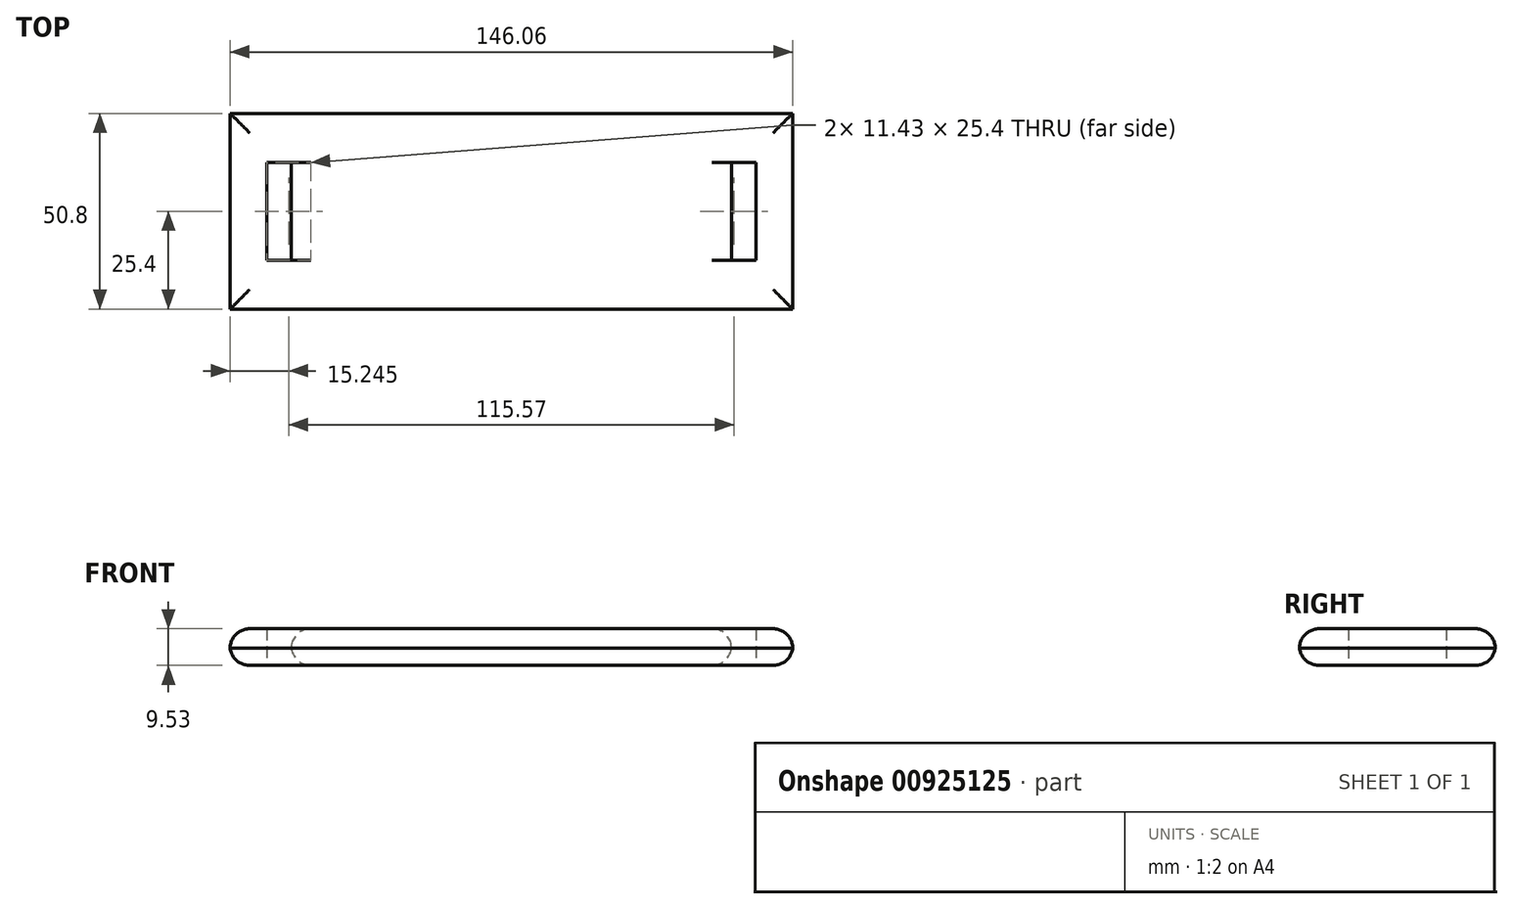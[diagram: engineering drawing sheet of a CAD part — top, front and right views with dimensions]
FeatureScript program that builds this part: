
annotation { "Feature Type Name" : "Feature", "Feature Type Description" : "" }
export const myFeature = defineFeature(function(context is Context, id is Id, definition is map)
    precondition{}
    {
        {
            var Q0;
            Q0=qCreatedBy(makeId("Top.planeOp"),FACE);
            var sketch = newSketch(context, id + "F0", { "sketchPlane" : qUnion([Q0])});
            skLineSegment(sketch, "E0.bottom", {"start": v(73.03, -25.4) * mm, "end": v(-73.03, -25.4) * mm});
            skLineSegment(sketch, "E0.top", {"start": v(73.03, 25.4) * mm, "end": v(-73.03, 25.4) * mm});
            skLineSegment(sketch, "E0.left", {"start": v(73.03, -25.4) * mm, "end": v(73.03, 25.4) * mm});
            skLineSegment(sketch, "E0.right", {"start": v(-73.03, -25.4) * mm, "end": v(-73.03, 25.4) * mm});
            skPoint(sketch, "E0.middle", {"position": v(0, 0) * mm});
            skLineSegment(sketch, "E1.bottom", {"start": v(-57.15, -12.7) * mm, "end": v(-63.5, -12.7) * mm});
            skLineSegment(sketch, "E1.top", {"start": v(-57.15, 12.7) * mm, "end": v(-63.5, 12.7) * mm});
            skLineSegment(sketch, "E1.left", {"start": v(-57.15, -12.7) * mm, "end": v(-57.15, 12.7) * mm});
            skLineSegment(sketch, "E1.right", {"start": v(-63.5, -12.7) * mm, "end": v(-63.5, 12.7) * mm});
            skPoint(sketch, "E1.middle", {"position": v(-60.33, 0) * mm});
            skLineSegment(sketch, "E2.bottom", {"start": v(63.5, -12.7) * mm, "end": v(57.15, -12.7) * mm});
            skLineSegment(sketch, "E2.top", {"start": v(63.5, 12.7) * mm, "end": v(57.15, 12.7) * mm});
            skLineSegment(sketch, "E2.left", {"start": v(63.5, -12.7) * mm, "end": v(63.5, 12.7) * mm});
            skLineSegment(sketch, "E2.right", {"start": v(57.15, -12.7) * mm, "end": v(57.15, 12.7) * mm});
            skPoint(sketch, "E2.middle", {"position": v(60.32, 0) * mm});
            skSolve(sketch);
        }
        {
            var Q0;
            Q0 = qSketchRegion(id + "F0", true);
            extrude(context, id + "F1", {"entities" : qUnion([Q0]), "depth" : 9.52 * mm, "offsetDistance" : 25.4 * mm});
        }
        {
            var Q0;
            Q0=makeQuery(id+"F1.opExtrude","CAP_EDGE",EDGE,{"disambiguationData":[OSD([sQuery(id+"F0.wireOp",EDGE,"E0.top")])],"isStart":false});
            var Q1;
            Q1=makeQuery(id+"F1.opExtrude","CAP_EDGE",EDGE,{"disambiguationData":[OSD([sQuery(id+"F0.wireOp",EDGE,"E0.left")])],"isStart":false});
            var Q2;
            Q2=makeQuery(id+"F1.opExtrude","CAP_EDGE",EDGE,{"disambiguationData":[OSD([sQuery(id+"F0.wireOp",EDGE,"E0.bottom")])],"isStart":false});
            var Q3;
            Q3=makeQuery(id+"F1.opExtrude","CAP_EDGE",EDGE,{"disambiguationData":[OSD([sQuery(id+"F0.wireOp",EDGE,"E0.right")])],"isStart":false});
            fillet(context, id + "F2", {"entities" : qUnion([Q0, Q1, Q2, Q3]), "radius" : 5.08 * mm, "tangentPropagation" : true, "allowEdgeOverflow" : false});
        }
        {
            var Q0;
            Q0=makeQuery(id+"F1.opExtrude","CAP_EDGE",EDGE,{"disambiguationData":[OSD([sQuery(id+"F0.wireOp",EDGE,"E0.bottom")])],"isStart":true});
            var Q1;
            Q1=makeQuery(id+"F1.opExtrude","CAP_EDGE",EDGE,{"disambiguationData":[OSD([sQuery(id+"F0.wireOp",EDGE,"E0.right")])],"isStart":true});
            var Q2;
            Q2=makeQuery(id+"F1.opExtrude","CAP_EDGE",EDGE,{"disambiguationData":[OSD([sQuery(id+"F0.wireOp",EDGE,"E0.top")])],"isStart":true});
            var Q3;
            Q3=makeQuery(id+"F1.opExtrude","CAP_EDGE",EDGE,{"disambiguationData":[OSD([sQuery(id+"F0.wireOp",EDGE,"E0.left")])],"isStart":true});
            var Q4;
            Q4=makeQuery(id+"F1.opExtrude","CAP_EDGE",EDGE,{"disambiguationData":[OSD([sQuery(id+"F0.wireOp",EDGE,"E2.right")])],"isStart":false});
            var Q5;
            Q5=makeQuery(id+"F1.opExtrude","CAP_EDGE",EDGE,{"disambiguationData":[OSD([sQuery(id+"F0.wireOp",EDGE,"E2.right")])],"isStart":true});
            var Q6;
            Q6=makeQuery(id+"F1.opExtrude","CAP_EDGE",EDGE,{"disambiguationData":[OSD([sQuery(id+"F0.wireOp",EDGE,"E1.left")])],"isStart":false});
            var Q7;
            Q7=makeQuery(id+"F1.opExtrude","CAP_EDGE",EDGE,{"disambiguationData":[OSD([sQuery(id+"F0.wireOp",EDGE,"E1.left")])],"isStart":true});
            fillet(context, id + "F3", {"entities" : qUnion([Q0, Q1, Q2, Q3, Q4, Q5, Q6, Q7]), "radius" : 5.08 * mm, "tangentPropagation" : true, "allowEdgeOverflow" : false});
        }
    });
